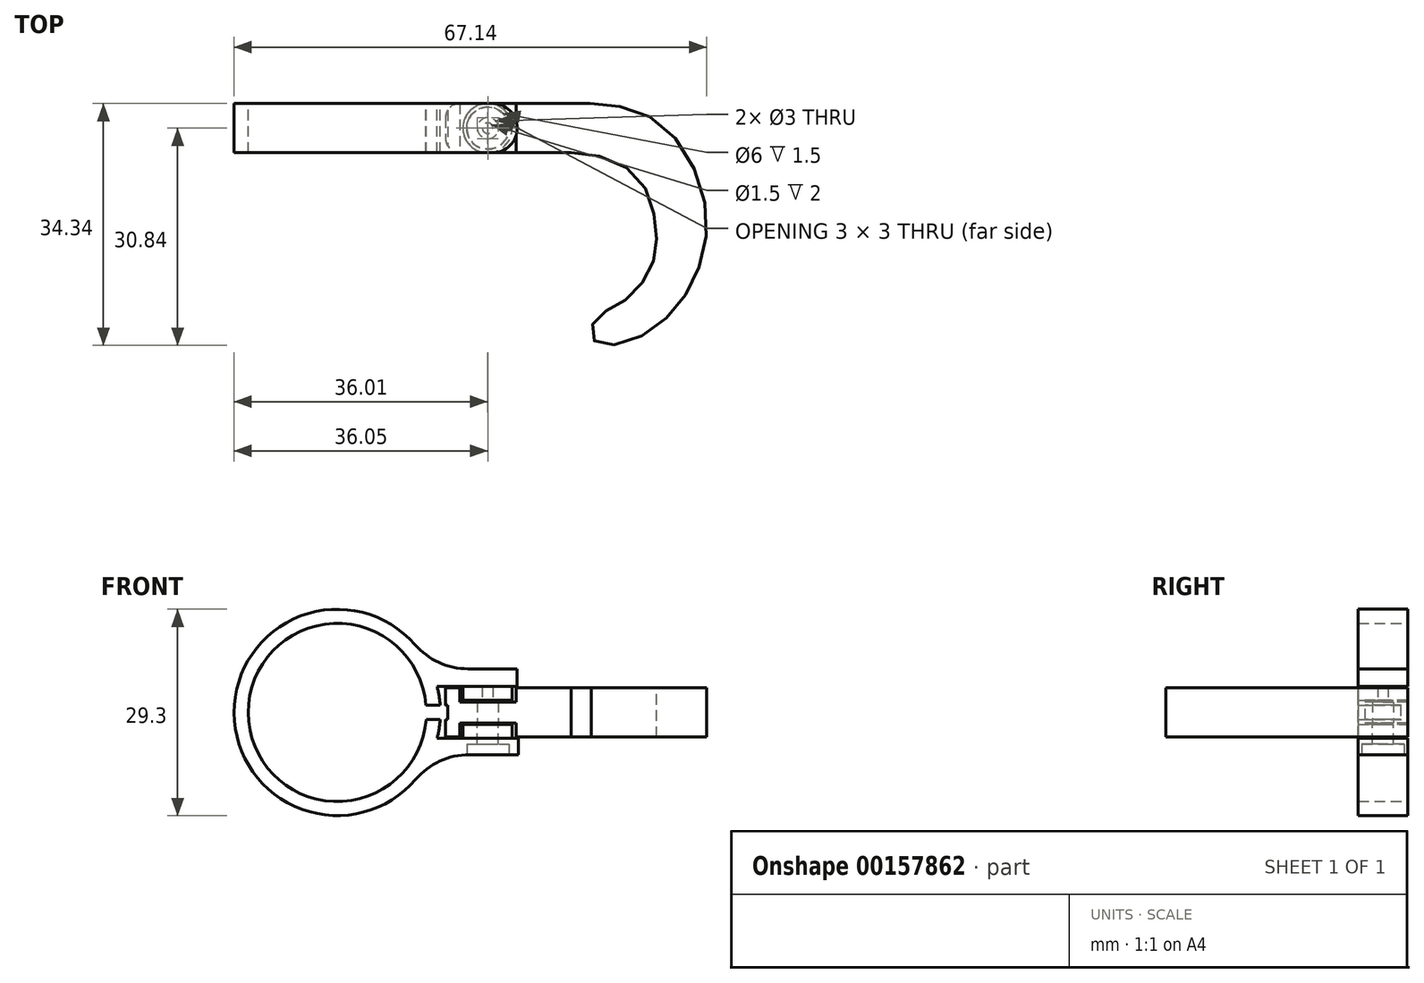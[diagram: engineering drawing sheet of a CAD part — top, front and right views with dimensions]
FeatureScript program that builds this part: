
annotation { "Feature Type Name" : "Feature", "Feature Type Description" : "" }
export const myFeature = defineFeature(function(context is Context, id is Id, definition is map)
    precondition{}
    {
        {
            var Q0;
            Q0=qCreatedBy(makeId("Top.planeOp"),FACE);
            var sketch = newSketch(context, id + "F0", { "sketchPlane" : qUnion([Q0])});
            skLineSegment(sketch, "E0", {"start": v(0, 0) * mm, "end": v(9, 0) * mm});
            skLineSegment(sketch, "E1", {"start": v(9, 0) * mm, "end": v(9, 0) * mm});
            skLineSegment(sketch, "E2", {"start": v(9, 0) * mm, "end": v(10.5, 0) * mm});
            skLineSegment(sketch, "E3", {"start": v(10.5, 0) * mm, "end": v(10.5, -7) * mm});
            skLineSegment(sketch, "E4", {"start": v(10.5, -7) * mm, "end": v(0, -7) * mm});
            skLineSegment(sketch, "E5", {"start": v(0, -7) * mm, "end": v(0, 0) * mm});
            skCircle(sketch, "E6", {"center": v(6, -3.5) * mm, "radius": 1.5 * mm});
            skLineSegment(sketch, "E7", {"start": v(10.5, 0) * mm, "end": v(20.5, 0) * mm});
            skFitSpline(sketch, "E8", {"points": [v(20.5, 0) * mm, v(30.68, -3.02) * mm, v(36.94, -14.98) * mm, v(34.8, -25.94) * mm, v(27.66, -33.07) * mm, v(21.18, -33.8) * mm, v(21.23, -30.7) * mm, v(25.2, -28.16) * mm, v(29.27, -23.03) * mm, v(29.81, -17.05) * mm, v(26.56, -9.75) * mm, v(17.85, -7) * mm], "startDerivative": vector(93.44, 0) * mm, "endDerivative": vector(-80.8, -1.43) * mm});
            skLineSegment(sketch, "E9", {"start": v(10.5, -7) * mm, "end": v(17.85, -7) * mm});
            skSolve(sketch);
        }
        {
            var Q0;
            Q0 = qSketchRegion(id + "F0", true);
            extrude(context, id + "F1", {"entities" : qUnion([Q0]), "depth" : 7 * mm});
        }
        {
            var Q0;
            Q0=makeQuery(id+"F1.opExtrude","CAP_FACE",FACE,{"disambiguationData":[OSD([sQuery(id+"F0.wireOp",EDGE,"E0"),sQuery(id+"F0.wireOp",EDGE,"E2"),sQuery(id+"F0.wireOp",EDGE,"E4"),sQuery(id+"F0.wireOp",EDGE,"CcRZLcxt-HltS-3Bgy-jA88-4HNwoiefxPg2"),sQuery(id+"F0.wireOp",EDGE,"qmqRNr1y-YMHt-ympM-1PT1-O91ouX4MxlrZ"),sQuery(id+"F0.wireOp",EDGE,"E5"),sQuery(id+"F0.wireOp",EDGE,"E6"),sQuery(id+"F0.wireOp",EDGE,"E7"),sQuery(id+"F0.wireOp",EDGE,"E8"),sQuery(id+"F0.wireOp",EDGE,"E9"),sQuery(id+"F0.wireOp",EDGE,"AUmqk3PW-EXc8-RmLv-jYep-wopp4y6gmSsj"),sQuery(id+"F0.wireOp",EDGE,"avpBQahv-7NwA-zZ0Y-nhRe-J0SHzzbZc8DR"),sQuery(id+"F0.wireOp",EDGE,"dtiyb2tF-2eEz-isbt-kbUT-tMJtYW1q9IoM")])],"isStart":true});
            var sketch = newSketch(context, id + "F2", { "sketchPlane" : qUnion([Q0])});
            skLineSegment(sketch, "E10", {"start": v(10, 0) * mm, "end": v(10, 7) * mm});
            skLineSegment(sketch, "E11", {"start": v(2, 0) * mm, "end": v(2, 7) * mm});
            skLineSegment(sketch, "E12", {"start": v(2, 7) * mm, "end": v(10, 7) * mm});
            skLineSegment(sketch, "E13", {"start": v(10, 0) * mm, "end": v(2, 0) * mm});
            skSolve(sketch);
        }
        {
            var Q0;
            Q0 = qSketchRegion(id + "F2", true);
            extrude(context, id + "F3", {"entities" : qUnion([Q0]), "operationType" : NewBodyOperationType.REMOVE, "oppositeDirection" : true, "depth" : 2 * mm});
        }
        {
            var Q0;
            Q0=makeQuery(id+"F1.opExtrude","CAP_FACE",FACE,{"disambiguationData":[OSD([sQuery(id+"F0.wireOp",EDGE,"E0"),sQuery(id+"F0.wireOp",EDGE,"E2"),sQuery(id+"F0.wireOp",EDGE,"E4"),sQuery(id+"F0.wireOp",EDGE,"E5"),sQuery(id+"F0.wireOp",EDGE,"E6"),sQuery(id+"F0.wireOp",EDGE,"E7"),sQuery(id+"F0.wireOp",EDGE,"E8"),sQuery(id+"F0.wireOp",EDGE,"E9")])],"isStart":false});
            var sketch = newSketch(context, id + "F4", { "sketchPlane" : qUnion([Q0])});
            skLineSegment(sketch, "E14.bottom", {"start": v(2, 0) * mm, "end": v(10, 0) * mm});
            skLineSegment(sketch, "E14.top", {"start": v(2, -7) * mm, "end": v(10, -7) * mm});
            skLineSegment(sketch, "E14.left", {"start": v(2, 0) * mm, "end": v(2, -7) * mm});
            skLineSegment(sketch, "E14.right", {"start": v(10, 0) * mm, "end": v(10, -7) * mm});
            skSolve(sketch);
        }
        {
            var Q0;
            Q0 = qSketchRegion(id + "F4", true);
            extrude(context, id + "F5", {"entities" : qUnion([Q0]), "operationType" : NewBodyOperationType.REMOVE, "oppositeDirection" : true, "depth" : 2 * mm});
        }
        {
            var Q0;
            Q0=qCreatedBy(makeId("Front.planeOp"),FACE);
            var sketch = newSketch(context, id + "F6", { "sketchPlane" : qUnion([Q0])});
            skCircle(sketch, "E15", {"center": v(-15.4, 3.5) * mm, "radius": 12.65 * mm});
            skCircle(sketch, "E16.0", {"center": v(-15.4, 3.5) * mm, "radius": 14.65 * mm});
            skLineSegment(sketch, "E17", {"start": v(-2.12, 9.7) * mm, "end": v(10.16, 9.7) * mm});
            skLineSegment(sketch, "E18", {"start": v(10.16, 9.7) * mm, "end": v(10.16, 7.2) * mm});
            skLineSegment(sketch, "E19", {"start": v(10.16, 7.2) * mm, "end": v(-1.22, 7.2) * mm});
            skLineSegment(sketch, "E20", {"start": v(-1.22, -0.2) * mm, "end": v(2, -0.2) * mm});
            skLineSegment(sketch, "E21", {"start": v(10.3, -2.5) * mm, "end": v(-2.03, -2.5) * mm});
            skLineSegment(sketch, "E22", {"start": v(2, -0.2) * mm, "end": v(10.3, -0.2) * mm});
            skLineSegment(sketch, "E23", {"start": v(10.3, -0.2) * mm, "end": v(10.3, -2.5) * mm});
            skSolve(sketch);
        }
        {
            var Q0;
            Q0 = qSketchRegion(id + "F6", true);
            extrude(context, id + "F7", {"entities" : qUnion([Q0]), "depth" : 7 * mm});
        }
        {
            var Q0;
            Q0=makeQuery(id+"F7.opExtrude","SWEPT_FACE",FACE,{"disambiguationData":[OSD([sQuery(id+"F6.wireOp",EDGE,"E20"),sQuery(id+"F6.wireOp",EDGE,"E22")])]});
            var sketch = newSketch(context, id + "F8", { "sketchPlane" : qUnion([Q0])});
            skCircle(sketch, "E24", {"center": v(5.94, -3.5) * mm, "radius": 3.5 * mm});
            skPoint(sketch, "E24.centerSnap0", {"position": v(10.3, -3.5) * mm});
            skSolve(sketch);
        }
        {
            var Q0;
            Q0 = qSketchRegion(id + "F8", true);
            extrude(context, id + "F9", {"entities" : qUnion([Q0]), "operationType" : NewBodyOperationType.ADD, "depth" : 2 * mm});
        }
        {
            var Q0;
            Q0=makeQuery(id+"F1.opExtrude","SWEPT_EDGE",EDGE,{"disambiguationData":[OSD([sQuery(id+"F0.wireOp",EDGE,"E4"),sQuery(id+"F0.wireOp",EDGE,"E5")])]});
            var Q1;
            Q1=makeQuery(id+"F1.opExtrude","SWEPT_EDGE",EDGE,{"disambiguationData":[OSD([sQuery(id+"F0.wireOp",EDGE,"E0"),sQuery(id+"F0.wireOp",EDGE,"E5")])]});
            fillet(context, id + "F10", {"entities" : qUnion([Q0, Q1]), "radius" : 2 * mm, "tangentPropagation" : true, "allowEdgeOverflow" : false});
        }
        {
            var Q0;
            Q0=makeQuery(id+"F7.opExtrude","SWEPT_EDGE",EDGE,{"disambiguationData":[OSD([sQuery(id+"F6.wireOp",EDGE,"E16.0"),sQuery(id+"F6.wireOp",EDGE,"E21")])]});
            var Q1;
            Q1=makeQuery(id+"F7.opExtrude","SWEPT_EDGE",EDGE,{"disambiguationData":[OSD([sQuery(id+"F6.wireOp",EDGE,"E16.0"),sQuery(id+"F6.wireOp",EDGE,"E17")])]});
            fillet(context, id + "F11", {"entities" : qUnion([Q0, Q1]), "radius" : 10 * mm, "tangentPropagation" : true, "allowEdgeOverflow" : false});
        }
        {
            var Q0;
            Q0=makeQuery(id+"F1.opExtrude","CAP_FACE",FACE,{"disambiguationData":[OSD([sQuery(id+"F0.wireOp",EDGE,"E0"),sQuery(id+"F0.wireOp",EDGE,"E2"),sQuery(id+"F0.wireOp",EDGE,"E4"),sQuery(id+"F0.wireOp",EDGE,"E5"),sQuery(id+"F0.wireOp",EDGE,"E6"),sQuery(id+"F0.wireOp",EDGE,"E7"),sQuery(id+"F0.wireOp",EDGE,"E8"),sQuery(id+"F0.wireOp",EDGE,"E9")])],"isStart":false});
            var sketch = newSketch(context, id + "F12", { "sketchPlane" : qUnion([Q0])});
            skCircle(sketch, "E25", {"center": v(6, -3.5) * mm, "radius": 1.5 * mm});
            skSolve(sketch);
        }
        {
            var Q0;
            Q0=makeQuery(id+"F7.opExtrude","CAP_EDGE",EDGE,{"disambiguationData":[OSD([sQuery(id+"F6.wireOp",EDGE,"E18")])],"isStart":true});
            var Q1;
            Q1=makeQuery(id+"F7.opExtrude","CAP_EDGE",EDGE,{"disambiguationData":[OSD([sQuery(id+"F6.wireOp",EDGE,"E18")])],"isStart":false});
            var Q2;
            Q2=makeQuery(id+"F7.opExtrude","CAP_EDGE",EDGE,{"disambiguationData":[OSD([sQuery(id+"F6.wireOp",EDGE,"E23")])],"isStart":true});
            var Q3;
            Q3=makeQuery(id+"F7.opExtrude","CAP_EDGE",EDGE,{"disambiguationData":[OSD([sQuery(id+"F6.wireOp",EDGE,"E23")])],"isStart":false});
            fillet(context, id + "F13", {"entities" : qUnion([Q0, Q1, Q2, Q3]), "radius" : 3.5 * mm, "tangentPropagation" : true, "allowEdgeOverflow" : false});
        }
        {
            var Q0;
            Q0 = qSketchRegion(id + "F12", true);
            var Q1;
            Q1=makeQuery(id+"F7.opExtrude","SWEPT_FACE",FACE,{"disambiguationData":[OSD([sQuery(id+"F6.wireOp",EDGE,"E21")])]});
            extrude(context, id + "F14", {"entities" : qUnion([Q0]), "operationType" : NewBodyOperationType.REMOVE, "endBound" : BoundingType.UP_TO_SURFACE, "oppositeDirection" : true, "endBoundEntityFace" : qUnion([Q1]), "depth" : 25 * mm});
        }
        {
            var Q0;
            Q0=makeQuery(id+"F7.opExtrude","CAP_FACE",FACE,{"disambiguationData":[OSD([sQuery(id+"F6.wireOp",EDGE,"E15"),sQuery(id+"F6.wireOp",EDGE,"E16.0"),sQuery(id+"F6.wireOp",EDGE,"E17"),sQuery(id+"F6.wireOp",EDGE,"E18"),sQuery(id+"F6.wireOp",EDGE,"E19"),sQuery(id+"F6.wireOp",EDGE,"E20"),sQuery(id+"F6.wireOp",EDGE,"E21"),sQuery(id+"F6.wireOp",EDGE,"E22"),sQuery(id+"F6.wireOp",EDGE,"E23")])],"isStart":false});
            var sketch = newSketch(context, id + "F15", { "sketchPlane" : qUnion([Q0])});
            skLineSegment(sketch, "E26", {"start": v(3.18, 9.7) * mm, "end": v(3.18, -2.5) * mm});
            skSolve(sketch);
        }
        {
            var Q0;
            Q0=makeQuery(id+"F15.imprint","IMPRINT",FACE,{"disambiguationData":[TD([[makeQuery(id+"F15.imprint","IMPRINT",EDGE,{"derivedFrom":makeQuery(id+"F7.opExtrude","CAP_EDGE",EDGE,{"disambiguationData":[OSD([sQuery(id+"F6.wireOp",EDGE,"E15")])],"isStart":false})}),1.0]])]});
            var sketch = newSketch(context, id + "F16", { "sketchPlane" : qUnion([Q0])});
            skLineSegment(sketch, "E27.bottom", {"start": v(-5.76, 4.53) * mm, "end": v(0.28, 4.53) * mm});
            skLineSegment(sketch, "E27.top", {"start": v(-5.76, 2.53) * mm, "end": v(0.28, 2.53) * mm});
            skLineSegment(sketch, "E27.left", {"start": v(-5.76, 4.53) * mm, "end": v(-5.76, 2.53) * mm});
            skLineSegment(sketch, "E27.right", {"start": v(0.28, 4.53) * mm, "end": v(0.28, 2.53) * mm});
            skSolve(sketch);
        }
        {
            var Q0;
            Q0 = qSketchRegion(id + "F16", true);
            extrude(context, id + "F17", {"entities" : qUnion([Q0]), "operationType" : NewBodyOperationType.REMOVE, "oppositeDirection" : true, "depth" : 25 * mm});
        }
        {
            var Q0;
            Q0=makeQuery(id+"F7.opExtrude","SWEPT_FACE",FACE,{"disambiguationData":[OSD([sQuery(id+"F6.wireOp",EDGE,"E21")])]});
            var sketch = newSketch(context, id + "F18", { "sketchPlane" : qUnion([Q0])});
            skCircle(sketch, "E28", {"center": v(6, 3.5) * mm, "radius": 3 * mm});
            skSolve(sketch);
        }
        {
            var Q0;
            Q0 = qSketchRegion(id + "F18", true);
            extrude(context, id + "F19", {"entities" : qUnion([Q0]), "operationType" : NewBodyOperationType.REMOVE, "oppositeDirection" : true, "depth" : 1.5 * mm});
        }
        {
            var Q0;
            Q0=makeQuery(id+"F7.opExtrude","SWEPT_FACE",FACE,{"disambiguationData":[OSD([sQuery(id+"F6.wireOp",EDGE,"E19")])]});
            var sketch = newSketch(context, id + "F20", { "sketchPlane" : qUnion([Q0])});
            skCircle(sketch, "E29", {"center": v(5.96, 3.5) * mm, "radius": 3.5 * mm});
            skPoint(sketch, "E29.centerSnap0", {"position": v(10.16, 3.5) * mm});
            skSolve(sketch);
        }
        {
            var Q0;
            Q0 = qSketchRegion(id + "F20", true);
            extrude(context, id + "F21", {"entities" : qUnion([Q0]), "operationType" : NewBodyOperationType.ADD, "depth" : 2 * mm});
        }
        {
            var Q0;
            Q0=makeQuery(id+"F21.opExtrude","CAP_FACE",FACE,{"disambiguationData":[OSD([sQuery(id+"F20.wireOp",EDGE,"E29")])],"isStart":false});
            var sketch = newSketch(context, id + "F22", { "sketchPlane" : qUnion([Q0])});
            skCircle(sketch, "E30", {"center": v(5.96, 3.5) * mm, "radius": 0.75 * mm});
            skSolve(sketch);
        }
        {
            var Q0;
            Q0 = qSketchRegion(id + "F22", true);
            extrude(context, id + "F23", {"entities" : qUnion([Q0]), "operationType" : NewBodyOperationType.REMOVE, "oppositeDirection" : true, "depth" : 2 * mm});
        }
    });
